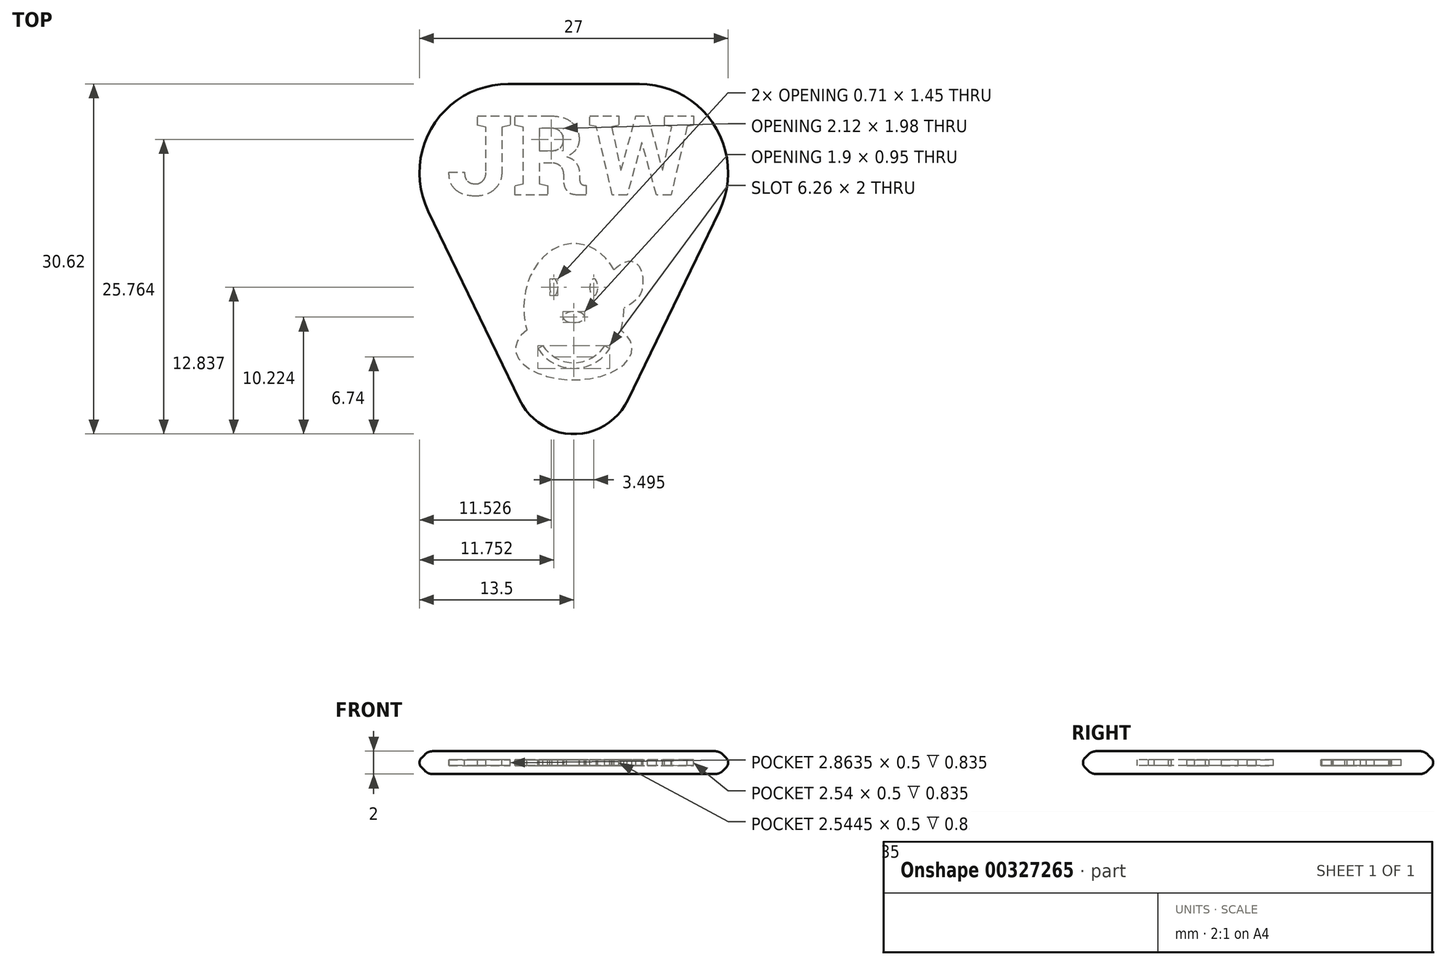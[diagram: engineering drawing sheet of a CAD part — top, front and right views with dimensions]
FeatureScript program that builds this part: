
annotation { "Feature Type Name" : "Feature", "Feature Type Description" : "" }
export const myFeature = defineFeature(function(context is Context, id is Id, definition is map)
    precondition{}
    {
        {
            var Q0;
            Q0=qCreatedBy(makeId("Top.planeOp"),FACE);
            var sketch = newSketch(context, id + "F0", { "sketchPlane" : qUnion([Q0])});
            skLineSegment(sketch, "E0", {"start": v(-5.74, 12.45) * mm, "end": v(5.74, 12.45) * mm});
            skLineSegment(sketch, "E1", {"start": v(12.95, 0.97) * mm, "end": v(4.95, -15.56) * mm});
            skLineSegment(sketch, "E2", {"start": v(-4.95, -15.56) * mm, "end": v(-12.95, 0.97) * mm});
            skPoint(sketch, "E3.visualSharp", {"position": v(-18.5, 12.45) * mm});
            skArc(sketch, "E3.filletArc", {"start": v(-5.74, 12.45) * mm, "mid": v(-12.52, 8.7) * mm, "end": v(-12.95, 0.97) * mm});
            skPoint(sketch, "E4.visualSharp", {"position": v(18.5, 12.45) * mm});
            skArc(sketch, "E4.filletArc", {"start": v(12.95, 0.97) * mm, "mid": v(12.52, 8.7) * mm, "end": v(5.74, 12.45) * mm});
            skPoint(sketch, "E5.visualSharp", {"position": v(0, -25.8) * mm});
            skArc(sketch, "E5.filletArc", {"start": v(-4.95, -15.56) * mm, "mid": v(0, -18.66) * mm, "end": v(4.95, -15.56) * mm});
            skSolve(sketch);
        }
        {
            var Q0;
            Q0=makeQuery(id+"F0.imprint","IMPRINT",FACE,{"disambiguationData":[TD([[makeQuery(id+"F0.imprint","IMPRINT",EDGE,{"derivedFrom":sQuery(id+"F0.wireOp",EDGE,"E0")}),-1.0]])]});
            extrude(context, id + "F1", {"entities" : qUnion([Q0]), "endBound" : BoundingType.SYMMETRIC, "depth" : 2 * mm});
        }
        {
            var Q0;
            Q0=makeQuery(id+"F1.opExtrude","CAP_EDGE",EDGE,{"disambiguationData":[OSD([sQuery(id+"F0.wireOp",EDGE,"E1")])],"isStart":false});
            var Q1;
            Q1=makeQuery(id+"F1.opExtrude","CAP_EDGE",EDGE,{"disambiguationData":[OSD([sQuery(id+"F0.wireOp",EDGE,"E1")])],"isStart":true});
            chamfer(context, id + "F2", {"entities" : qUnion([Q0, Q1]), "chamferType" : ChamferType.OFFSET_ANGLE, "width" : 1 * mm, "oppositeDirection" : false, "angle" : 45 * degree, "tangentPropagation" : true});
        }
        {
            var Q0;
            {var subQ0=sQuery(id+"F0.wireOp",EDGE,"E2");Q0=makeQuery(id+"F2.opChamfer","BLEND_EDGE",EDGE,{"blendedFrom":[makeQuery(id+"F1.opExtrude","CAP_EDGE",EDGE,{"disambiguationData":[OSD([subQ0])],"isStart":false}),makeQuery(id+"F1.opExtrude","CAP_FACE",FACE,{"disambiguationData":[OSD([sQuery(id+"F0.wireOp",EDGE,"E0"),sQuery(id+"F0.wireOp",EDGE,"E1"),subQ0,sQuery(id+"F0.wireOp",EDGE,"E3.filletArc"),sQuery(id+"F0.wireOp",EDGE,"E4.filletArc"),sQuery(id+"F0.wireOp",EDGE,"E5.filletArc")])],"isStart":false})],"blendedInto":[makeQuery(id+"F1.opExtrude","CAP_FACE",FACE,{"disambiguationData":[OSD([sQuery(id+"F0.wireOp",EDGE,"E0"),sQuery(id+"F0.wireOp",EDGE,"E1"),subQ0,sQuery(id+"F0.wireOp",EDGE,"E3.filletArc"),sQuery(id+"F0.wireOp",EDGE,"E4.filletArc"),sQuery(id+"F0.wireOp",EDGE,"E5.filletArc")])],"isStart":false})]});}
            var Q1;
            {var subQ0=sQuery(id+"F0.wireOp",EDGE,"E1");Q1=makeQuery(id+"F2.opChamfer","BLEND_EDGE",EDGE,{"blendedFrom":[makeQuery(id+"F1.opExtrude","CAP_EDGE",EDGE,{"disambiguationData":[OSD([subQ0])],"isStart":true}),makeQuery(id+"F1.opExtrude","CAP_FACE",FACE,{"disambiguationData":[OSD([sQuery(id+"F0.wireOp",EDGE,"E0"),subQ0,sQuery(id+"F0.wireOp",EDGE,"E2"),sQuery(id+"F0.wireOp",EDGE,"E3.filletArc"),sQuery(id+"F0.wireOp",EDGE,"E4.filletArc"),sQuery(id+"F0.wireOp",EDGE,"E5.filletArc")])],"isStart":true})],"blendedInto":[makeQuery(id+"F1.opExtrude","CAP_FACE",FACE,{"disambiguationData":[OSD([sQuery(id+"F0.wireOp",EDGE,"E0"),subQ0,sQuery(id+"F0.wireOp",EDGE,"E2"),sQuery(id+"F0.wireOp",EDGE,"E3.filletArc"),sQuery(id+"F0.wireOp",EDGE,"E4.filletArc"),sQuery(id+"F0.wireOp",EDGE,"E5.filletArc")])],"isStart":true})]});}
            fillet(context, id + "F3", {"entities" : qUnion([Q0, Q1]), "radius" : 1 * mm, "tangentPropagation" : true, "allowEdgeOverflow" : false});
        }
        {
            var Q0;
            Q0=qCreatedBy(makeId("Top.planeOp"),FACE);
            var sketch = newSketch(context, id + "F4", { "sketchPlane" : qUnion([Q0])});
            skText(sketch, "E6", { "text": "JRW", "fontName": "RobotoSlab-Bold.ttf"});
            const initialGuessF4  = {"E6": [-0.01108, 0.0025, 1, 0, 0.007]};
            skSetInitialGuess(sketch, initialGuessF4);
            skSolve(sketch);
        }
        {
            var Q0;
            Q0=qSketchRegion(id+"F4",true);
            extrude(context, id + "F5", {"entities" : qUnion([Q0]), "operationType" : NewBodyOperationType.REMOVE, "endBound" : BoundingType.SYMMETRIC, "oppositeDirection" : true, "depth" : 0.5 * mm});
        }
        {
            var Q0;
            {var subQ0=sQuery(id+"F0.wireOp",EDGE,"E2");Q0=makeQuery(id+"F2.opChamfer","BLEND_EDGE",EDGE,{"blendedFrom":[makeQuery(id+"F1.opExtrude","CAP_EDGE",EDGE,{"disambiguationData":[OSD([subQ0])],"isStart":true}),makeQuery(id+"F1.opExtrude","CAP_EDGE",EDGE,{"disambiguationData":[OSD([subQ0])],"isStart":false})],"blendedInto":[]});}
            fillet(context, id + "F6", {"entities" : qUnion([Q0]), "radius" : 0.6 * mm, "tangentPropagation" : true, "allowEdgeOverflow" : false});
        }
        {
            var Q0;
            Q0=qCreatedBy(makeId("Top.planeOp"),FACE);
            var sketch = newSketch(context, id + "F7", { "sketchPlane" : qUnion([Q0])});
            skEllipticalArc(sketch, "E7", {});
            skEllipticalArc(sketch, "E8", {});
            skFitSpline(sketch, "E9", {"points": [v(3.52, -4.04) * mm, v(4.55, -3.34) * mm, v(5.62, -3.64) * mm, v(5.88, -6.04) * mm, v(4.38, -7.39) * mm], "startDerivative": vector(4.44, 4.1) * mm, "endDerivative": vector(-6.73, -3.64) * mm});
            skFitSpline(sketch, "E10.MirrorCS", {"points": [v(-3.52, -4.04) * mm, v(-4.55, -3.34) * mm, v(-5.62, -3.64) * mm, v(-5.88, -6.04) * mm, v(-4.38, -7.39) * mm], "startDerivative": vector(-4.44, 4.1) * mm, "endDerivative": vector(6.73, -3.64) * mm});
            skEllipse(sketch, "E11", {"center": v(1.75, -5.57) * mm, "majorRadius": 0.72 * mm, "minorRadius": 0.36 * mm, "majorAxis": v(0, -1)});
            skEllipse(sketch, "E12", {"center": v(0, -8.19) * mm, "majorRadius": 0.95 * mm, "minorRadius": 0.47 * mm, "majorAxis": v(1, 0)});
            skEllipse(sketch, "E13.MirrorC", {"center": v(-1.75, -5.57) * mm, "majorRadius": 0.72 * mm, "minorRadius": 0.36 * mm, "majorAxis": v(0, -1)});
            skFitSpline(sketch, "E14", {"points": [v(0, -4.04) * mm, v(-1.55, -3.67) * mm, v(-2.93, -4.58) * mm, v(-2.7, -8.6) * mm], "startDerivative": vector(-5.51, 2.21) * mm, "endDerivative": vector(2.18, -10.68) * mm});
            skFitSpline(sketch, "E15.MirrorCS", {"points": [v(0, -4.04) * mm, v(1.55, -3.67) * mm, v(2.93, -4.58) * mm, v(2.7, -8.6) * mm], "startDerivative": vector(5.51, 2.21) * mm, "endDerivative": vector(-2.18, -10.68) * mm});
            skArc(sketch, "E16", {"start": v(3.13, -10.93) * mm, "mid": v(1.8, -12.2) * mm, "end": v(0, -12.67) * mm});
            skArc(sketch, "E17.MirrorCS", {"start": v(-3.13, -10.93) * mm, "mid": v(-1.8, -12.2) * mm, "end": v(0, -12.67) * mm});
            skArc(sketch, "E18.0", {"start": v(-2.7, -10.67) * mm, "mid": v(-1.55, -11.77) * mm, "end": v(0, -12.17) * mm});
            skArc(sketch, "E19.MirrorCS", {"start": v(2.7, -10.67) * mm, "mid": v(1.55, -11.77) * mm, "end": v(0, -12.17) * mm});
            skLineSegment(sketch, "E20", {"start": v(-3.13, -10.93) * mm, "end": v(-2.7, -10.67) * mm});
            skLineSegment(sketch, "E21", {"start": v(2.7, -10.67) * mm, "end": v(3.13, -10.93) * mm});
            skFitSpline(sketch, "E22.0", {"points": [v(-0.98, -13.43) * mm, v(0, -13.55) * mm, v(0.98, -13.43) * mm, v(1.91, -13.06) * mm, v(2.77, -12.47) * mm, v(3.5, -11.7) * mm, v(4.1, -10.77) * mm, v(4.53, -9.7) * mm, v(4.8, -8.57) * mm, v(4.89, -7.39) * mm, v(4.8, -6.2) * mm, v(4.53, -5.07) * mm, v(4.1, -4.01) * mm, v(3.5, -3.08) * mm, v(2.77, -2.3) * mm, v(1.91, -1.72) * mm, v(0.98, -1.35) * mm, v(0, -1.23) * mm, v(-0.98, -1.35) * mm, v(-1.91, -1.72) * mm, v(-2.77, -2.3) * mm, v(-3.5, -3.08) * mm, v(-4.1, -4.01) * mm, v(-4.53, -5.07) * mm, v(-4.8, -6.2) * mm, v(-4.89, -7.39) * mm, v(-4.8, -8.57) * mm, v(-4.53, -9.7) * mm, v(-4.1, -10.77) * mm, v(-3.5, -11.7) * mm, v(-2.77, -12.47) * mm, v(-1.91, -13.06) * mm, v(-0.98, -13.43) * mm, v(0, -13.55) * mm, v(0.98, -13.43) * mm]});
            skLineSegment(sketch, "E23", {"start": v(-4.58, -9.43) * mm, "end": v(-4.51, -9.67) * mm});
            skLineSegment(sketch, "E24.MirrorCS", {"start": v(4.58, -9.43) * mm, "end": v(4.51, -9.67) * mm});
            const initialGuessF7  = {"E7": [1.3970180617640192e-08, -0.007389856315825704, 0, -1, 0.005639855284243822, 0.0043772660306950735, 1.2220849475554958, 5.061097125015299], "E8": [0, -0.010932845994830132, 1, 0, 0.005087355151772499, 0.002746738975732119, 2.1312338919539324, 1.0103587616358605]};
            skSetInitialGuess(sketch, initialGuessF7);
            skSolve(sketch);
        }
        {
            var Q0;
            Q0=qSketchRegion(id+"F7",true);
            var Q1;
            Q1=makeQuery(id+"F7.imprint","IMPRINT",FACE,{"disambiguationData":[TD([[makeQuery(id+"F7.imprint","IMPRINT",EDGE,{"derivedFrom":sQuery(id+"F7.wireOp",EDGE,"b4bf5cf7-47f6-4e07-859f-e1e6065c9dbf.0")}),-1.0]])]});
            var Q2;
            Q2=makeQuery(id+"F7.imprint","IMPRINT",FACE,{"disambiguationData":[TD([[makeQuery(id+"F7.imprint","IMPRINT",EDGE,{"derivedFrom":sQuery(id+"F7.wireOp",EDGE,"6f85d2ec-8929-457e-84c4-58013a10ac05.0")}),-1.0]])]});
            extrude(context, id + "F8", {"entities" : qUnion([Q0, Q1, Q2]), "operationType" : NewBodyOperationType.REMOVE, "endBound" : BoundingType.SYMMETRIC, "oppositeDirection" : true, "depth" : 0.5 * mm, "offsetDistance" : 25 * mm});
        }
    });
